# Revit family: EL-LF-HH4532A2AHN_()0000003062_Facebased_ver-2-0_2022_tsuujou_LDL40TN1725G3
name_source: partatom
category: 照明器具
units: mm (PartAtom-declared; Revit-internal decimal feet)

## family parameters
パーツ タイプ = 標準
ホスト = 面
ロード時にボイドで切り取り = いいえ
丸型コネクタ寸法 = 直径を使用
光源 = いいえ
共有 = いいえ
注釈の向きを維持 = いいえ
部屋計算ポイント = いいえ

## types (1)
- _固定出力_初期照度補正機能搭載なし__
    Clearance Back = 0  [stored 0 ft]
    Clearance Bottom = 0  [stored 0 ft]
    Clearance Front = 0  [stored 0 ft]
    Clearance Left = 0  [stored 0 ft]
    Clearance Right = 0  [stored 0 ft]
    Clearance Top = 0  [stored 0 ft]
    Depth = 215  [stored 0.705381 ft]
    Height = 108  [stored 0.354331 ft]
    IfcExportAs = IfcLightFixtureType
    LED制御装置 = 一般形(LN)
    URL = https://www.mitsubishielectric.co.jp
    Width = 1248  [stored 4.09449 ft]
    コンバート開始日時 = 2023年09月08日(金) 11時16分19秒242
    サービススペース = いいえ
    モデル = EL-LF-HH4532A/2 AHN
    ランプ = LDL40T･N/17/25･G3
    ランプ_全光束 = 5000 lm
    ランプ_定格消費効率(lm/W) = 0
    ランプ_定格消費電力 = 0.0 W
    ランプ_本数 = 2
    ランプ_電流 = 0.000 A
    企業コード = 118713
    保守率(1)良いのコメント = 保守率良いの場合：0.88
    保守率(2)普通のコメント = 保守率普通の場合：0.86
    保守率(3)悪いのコメント = 保守率悪いの場合：0.81
    入力電圧1(電圧指定=1) = 100 V
    入力電圧2(電圧指定=2) = 200 V
    入力電圧3(電圧指定=3) = 242 V
    入力電流1 = 0.430 A
    入力電流2 = 0.220 A
    入力電流3 = 0.180 A
    分類コード = 40300000000000
    周波数 = 0 Hz
    呼称 = Lﾌｧｲﾝecoｼﾘｰｽﾞ非常灯
    固有エネルギー消費効率(lm/W) = 32.857143
    安定器_二次電圧 = 0 V
    安定器_入力電力 = 0.0 W
    安定器_入力電流 = 0.000 A
    安定器_定格電圧 = 0 V
    定格光束 = 0 lm
    定格入力容量 = 43 VA
    定格入力電圧 = 100 V
    定格入力電流 = 0.430 A
    定格消費電力 = 42.0 W
    平均演色評価数(Ra) = 83
    形式 = 笠付
    既定の高さ = 1219
    材質_カバー = <カテゴリ別>
    材質_ルーバー = <カテゴリ別>
    材質_反射板 = <カテゴリ別>
    材質_本体 = <カテゴリ別>
    極数 = 1
    消費電力1 = 42.0 W
    消費電力2 = 42.0 W
    消費電力3 = 42.0 W
    皮相負荷 = 43 VA
    直径 = 0  [stored 0 ft]
    相 = 1
    積算_科目 = 1 電灯設備
    製品質量 = 0.00 kg
    製造元 = 三菱電機照明株式会社
    設置方法 = 直付
    質量 = 0.00 kg
    運転質量 = 0.00 kg
    配光角 = 0
    開口部寸法(奥行) = 0  [stored 0 ft]
    開口部寸法(幅) = 0  [stored 0 ft]
    開口部寸法(径) = 0  [stored 0 ft]
    電圧指定 = 1

note: [stored X ft] marks values corroborated as IEEE doubles in the binary element streams (Revit-internal decimal feet)
